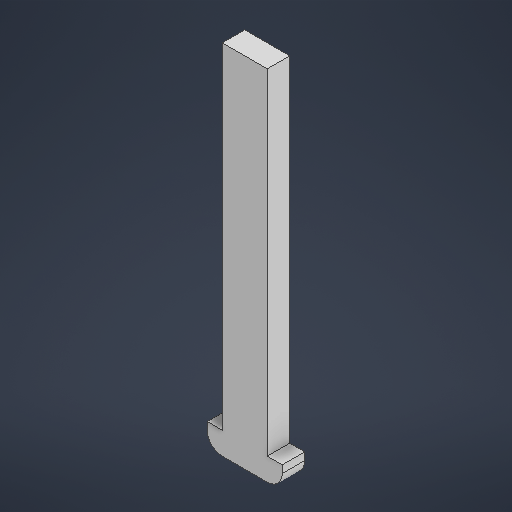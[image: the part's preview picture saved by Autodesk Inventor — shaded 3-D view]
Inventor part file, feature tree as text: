
AUTODESK INVENTOR PART (.ipt)
format: ipt  version: 2025.3 (Build 293356030, 356C)  size: 194,560 bytes
history: native  units: mm
features: other x1, extrude x1, sketch x1
ambient origin geometry x8: Origin, YZ Plane, XZ Plane, XY Plane, X Axis, Y Axis, Z Axis, Center Point
bodies: Body1 (feature_tree)
feature tree (3):
  other  "實體1"
  extrude  "擠出1"  Depth=6.0mm
  sketch  "草圖1"
